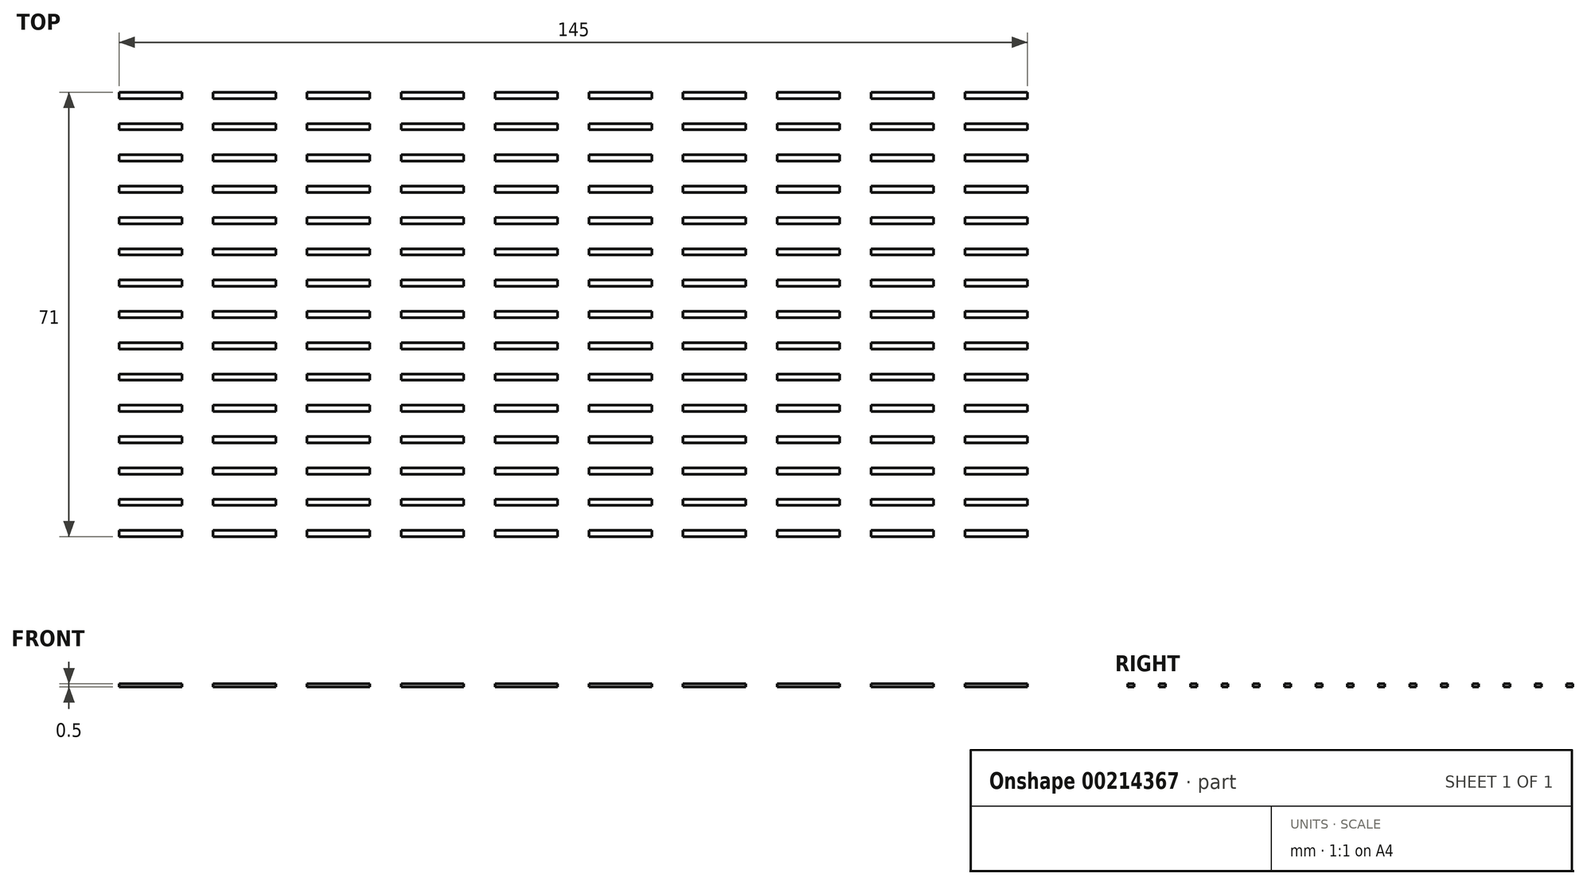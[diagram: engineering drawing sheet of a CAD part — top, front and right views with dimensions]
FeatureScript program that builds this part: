
annotation { "Feature Type Name" : "Feature", "Feature Type Description" : "" }
export const myFeature = defineFeature(function(context is Context, id is Id, definition is map)
    precondition{}
    {
        {
            var Q0;
            Q0=qCreatedBy(makeId("Top.planeOp"),FACE);
            var sketch = newSketch(context, id + "F0", { "sketchPlane" : qUnion([Q0])});
            skLineSegment(sketch, "E0.bottom", {"start": v(0, 0) * mm, "end": v(10, 0) * mm});
            skLineSegment(sketch, "E0.top", {"start": v(0, 1) * mm, "end": v(10, 1) * mm});
            skLineSegment(sketch, "E0.left", {"start": v(0, 0) * mm, "end": v(0, 1) * mm});
            skLineSegment(sketch, "E0.right", {"start": v(10, 0) * mm, "end": v(10, 1) * mm});
            skLineSegment(sketch, "E1.0.1.0", {"start": v(0, 6) * mm, "end": v(10, 6) * mm});
            skLineSegment(sketch, "E1.0.1.1", {"start": v(0, 5) * mm, "end": v(0, 6) * mm});
            skLineSegment(sketch, "E1.0.1.2", {"start": v(10, 5) * mm, "end": v(10, 6) * mm});
            skLineSegment(sketch, "E1.0.1.3", {"start": v(0, 5) * mm, "end": v(10, 5) * mm});
            skLineSegment(sketch, "E1.1.0.0", {"start": v(15, 1) * mm, "end": v(25, 1) * mm});
            skLineSegment(sketch, "E1.1.0.1", {"start": v(15, 0) * mm, "end": v(15, 1) * mm});
            skLineSegment(sketch, "E1.1.0.2", {"start": v(25, 0) * mm, "end": v(25, 1) * mm});
            skLineSegment(sketch, "E1.1.0.3", {"start": v(15, 0) * mm, "end": v(25, 0) * mm});
            skLineSegment(sketch, "E1.1.1.0", {"start": v(15, 6) * mm, "end": v(25, 6) * mm});
            skLineSegment(sketch, "E1.1.1.1", {"start": v(15, 5) * mm, "end": v(15, 6) * mm});
            skLineSegment(sketch, "E1.1.1.2", {"start": v(25, 5) * mm, "end": v(25, 6) * mm});
            skLineSegment(sketch, "E1.1.1.3", {"start": v(15, 5) * mm, "end": v(25, 5) * mm});
            skLineSegment(sketch, "E1.2.0.0", {"start": v(30, 1) * mm, "end": v(40, 1) * mm});
            skLineSegment(sketch, "E1.2.0.1", {"start": v(30, 0) * mm, "end": v(30, 1) * mm});
            skLineSegment(sketch, "E1.2.0.2", {"start": v(40, 0) * mm, "end": v(40, 1) * mm});
            skLineSegment(sketch, "E1.2.0.3", {"start": v(30, 0) * mm, "end": v(40, 0) * mm});
            skLineSegment(sketch, "E1.2.1.0", {"start": v(30, 6) * mm, "end": v(40, 6) * mm});
            skLineSegment(sketch, "E1.2.1.1", {"start": v(30, 5) * mm, "end": v(30, 6) * mm});
            skLineSegment(sketch, "E1.2.1.2", {"start": v(40, 5) * mm, "end": v(40, 6) * mm});
            skLineSegment(sketch, "E1.2.1.3", {"start": v(30, 5) * mm, "end": v(40, 5) * mm});
            skLineSegment(sketch, "E1.direction1", {"start": v(0, 0) * mm, "end": v(15, 0) * mm, "construction": true});
            skLineSegment(sketch, "E1.direction2", {"start": v(0, 0) * mm, "end": v(0, 5) * mm, "construction": true});
            skLineSegment(sketch, "E2.0.3.0", {"start": v(45, 1) * mm, "end": v(55, 1) * mm});
            skLineSegment(sketch, "E2.3.3.0", {"start": v(45, 0) * mm, "end": v(45, 1) * mm});
            skLineSegment(sketch, "E2.6.3.0", {"start": v(55, 0) * mm, "end": v(55, 1) * mm});
            skLineSegment(sketch, "E2.9.3.0", {"start": v(45, 0) * mm, "end": v(55, 0) * mm});
            skLineSegment(sketch, "E2.0.3.1", {"start": v(45, 6) * mm, "end": v(55, 6) * mm});
            skLineSegment(sketch, "E2.3.3.1", {"start": v(45, 5) * mm, "end": v(45, 6) * mm});
            skLineSegment(sketch, "E2.6.3.1", {"start": v(55, 5) * mm, "end": v(55, 6) * mm});
            skLineSegment(sketch, "E2.9.3.1", {"start": v(45, 5) * mm, "end": v(55, 5) * mm});
            skLineSegment(sketch, "E2.0.4.0", {"start": v(60, 1) * mm, "end": v(70, 1) * mm});
            skLineSegment(sketch, "E2.3.4.0", {"start": v(60, 0) * mm, "end": v(60, 1) * mm});
            skLineSegment(sketch, "E2.6.4.0", {"start": v(70, 0) * mm, "end": v(70, 1) * mm});
            skLineSegment(sketch, "E2.9.4.0", {"start": v(60, 0) * mm, "end": v(70, 0) * mm});
            skLineSegment(sketch, "E2.0.4.1", {"start": v(60, 6) * mm, "end": v(70, 6) * mm});
            skLineSegment(sketch, "E2.3.4.1", {"start": v(60, 5) * mm, "end": v(60, 6) * mm});
            skLineSegment(sketch, "E2.6.4.1", {"start": v(70, 5) * mm, "end": v(70, 6) * mm});
            skLineSegment(sketch, "E2.9.4.1", {"start": v(60, 5) * mm, "end": v(70, 5) * mm});
            skLineSegment(sketch, "E2.0.5.0", {"start": v(75, 1) * mm, "end": v(85, 1) * mm});
            skLineSegment(sketch, "E2.3.5.0", {"start": v(75, 0) * mm, "end": v(75, 1) * mm});
            skLineSegment(sketch, "E2.6.5.0", {"start": v(85, 0) * mm, "end": v(85, 1) * mm});
            skLineSegment(sketch, "E2.9.5.0", {"start": v(75, 0) * mm, "end": v(85, 0) * mm});
            skLineSegment(sketch, "E2.0.5.1", {"start": v(75, 6) * mm, "end": v(85, 6) * mm});
            skLineSegment(sketch, "E2.3.5.1", {"start": v(75, 5) * mm, "end": v(75, 6) * mm});
            skLineSegment(sketch, "E2.6.5.1", {"start": v(85, 5) * mm, "end": v(85, 6) * mm});
            skLineSegment(sketch, "E2.9.5.1", {"start": v(75, 5) * mm, "end": v(85, 5) * mm});
            skLineSegment(sketch, "E2.0.6.0", {"start": v(90, 1) * mm, "end": v(100, 1) * mm});
            skLineSegment(sketch, "E2.3.6.0", {"start": v(90, 0) * mm, "end": v(90, 1) * mm});
            skLineSegment(sketch, "E2.6.6.0", {"start": v(100, 0) * mm, "end": v(100, 1) * mm});
            skLineSegment(sketch, "E2.9.6.0", {"start": v(90, 0) * mm, "end": v(100, 0) * mm});
            skLineSegment(sketch, "E2.0.6.1", {"start": v(90, 6) * mm, "end": v(100, 6) * mm});
            skLineSegment(sketch, "E2.3.6.1", {"start": v(90, 5) * mm, "end": v(90, 6) * mm});
            skLineSegment(sketch, "E2.6.6.1", {"start": v(100, 5) * mm, "end": v(100, 6) * mm});
            skLineSegment(sketch, "E2.9.6.1", {"start": v(90, 5) * mm, "end": v(100, 5) * mm});
            skLineSegment(sketch, "E2.0.7.0", {"start": v(105, 1) * mm, "end": v(115, 1) * mm});
            skLineSegment(sketch, "E2.3.7.0", {"start": v(105, 0) * mm, "end": v(105, 1) * mm});
            skLineSegment(sketch, "E2.6.7.0", {"start": v(115, 0) * mm, "end": v(115, 1) * mm});
            skLineSegment(sketch, "E2.9.7.0", {"start": v(105, 0) * mm, "end": v(115, 0) * mm});
            skLineSegment(sketch, "E2.0.7.1", {"start": v(105, 6) * mm, "end": v(115, 6) * mm});
            skLineSegment(sketch, "E2.3.7.1", {"start": v(105, 5) * mm, "end": v(105, 6) * mm});
            skLineSegment(sketch, "E2.6.7.1", {"start": v(115, 5) * mm, "end": v(115, 6) * mm});
            skLineSegment(sketch, "E2.9.7.1", {"start": v(105, 5) * mm, "end": v(115, 5) * mm});
            skLineSegment(sketch, "E2.0.8.0", {"start": v(120, 1) * mm, "end": v(130, 1) * mm});
            skLineSegment(sketch, "E2.3.8.0", {"start": v(120, 0) * mm, "end": v(120, 1) * mm});
            skLineSegment(sketch, "E2.6.8.0", {"start": v(130, 0) * mm, "end": v(130, 1) * mm});
            skLineSegment(sketch, "E2.9.8.0", {"start": v(120, 0) * mm, "end": v(130, 0) * mm});
            skLineSegment(sketch, "E2.0.8.1", {"start": v(120, 6) * mm, "end": v(130, 6) * mm});
            skLineSegment(sketch, "E2.3.8.1", {"start": v(120, 5) * mm, "end": v(120, 6) * mm});
            skLineSegment(sketch, "E2.6.8.1", {"start": v(130, 5) * mm, "end": v(130, 6) * mm});
            skLineSegment(sketch, "E2.9.8.1", {"start": v(120, 5) * mm, "end": v(130, 5) * mm});
            skLineSegment(sketch, "E2.0.9.0", {"start": v(135, 1) * mm, "end": v(145, 1) * mm});
            skLineSegment(sketch, "E2.3.9.0", {"start": v(135, 0) * mm, "end": v(135, 1) * mm});
            skLineSegment(sketch, "E2.6.9.0", {"start": v(145, 0) * mm, "end": v(145, 1) * mm});
            skLineSegment(sketch, "E2.9.9.0", {"start": v(135, 0) * mm, "end": v(145, 0) * mm});
            skLineSegment(sketch, "E2.0.9.1", {"start": v(135, 6) * mm, "end": v(145, 6) * mm});
            skLineSegment(sketch, "E2.3.9.1", {"start": v(135, 5) * mm, "end": v(135, 6) * mm});
            skLineSegment(sketch, "E2.6.9.1", {"start": v(145, 5) * mm, "end": v(145, 6) * mm});
            skLineSegment(sketch, "E2.9.9.1", {"start": v(135, 5) * mm, "end": v(145, 5) * mm});
            skLineSegment(sketch, "E3.0.0.2", {"start": v(0, 11) * mm, "end": v(10, 11) * mm});
            skLineSegment(sketch, "E3.3.0.2", {"start": v(0, 10) * mm, "end": v(0, 11) * mm});
            skLineSegment(sketch, "E3.6.0.2", {"start": v(10, 10) * mm, "end": v(10, 11) * mm});
            skLineSegment(sketch, "E3.9.0.2", {"start": v(0, 10) * mm, "end": v(10, 10) * mm});
            skLineSegment(sketch, "E3.0.0.3", {"start": v(0, 16) * mm, "end": v(10, 16) * mm});
            skLineSegment(sketch, "E3.3.0.3", {"start": v(0, 15) * mm, "end": v(0, 16) * mm});
            skLineSegment(sketch, "E3.6.0.3", {"start": v(10, 15) * mm, "end": v(10, 16) * mm});
            skLineSegment(sketch, "E3.9.0.3", {"start": v(0, 15) * mm, "end": v(10, 15) * mm});
            skLineSegment(sketch, "E3.0.0.4", {"start": v(0, 21) * mm, "end": v(10, 21) * mm});
            skLineSegment(sketch, "E3.3.0.4", {"start": v(0, 20) * mm, "end": v(0, 21) * mm});
            skLineSegment(sketch, "E3.6.0.4", {"start": v(10, 20) * mm, "end": v(10, 21) * mm});
            skLineSegment(sketch, "E3.9.0.4", {"start": v(0, 20) * mm, "end": v(10, 20) * mm});
            skLineSegment(sketch, "E3.0.0.5", {"start": v(0, 26) * mm, "end": v(10, 26) * mm});
            skLineSegment(sketch, "E3.3.0.5", {"start": v(0, 25) * mm, "end": v(0, 26) * mm});
            skLineSegment(sketch, "E3.6.0.5", {"start": v(10, 25) * mm, "end": v(10, 26) * mm});
            skLineSegment(sketch, "E3.9.0.5", {"start": v(0, 25) * mm, "end": v(10, 25) * mm});
            skLineSegment(sketch, "E3.0.0.6", {"start": v(0, 31) * mm, "end": v(10, 31) * mm});
            skLineSegment(sketch, "E3.3.0.6", {"start": v(0, 30) * mm, "end": v(0, 31) * mm});
            skLineSegment(sketch, "E3.6.0.6", {"start": v(10, 30) * mm, "end": v(10, 31) * mm});
            skLineSegment(sketch, "E3.9.0.6", {"start": v(0, 30) * mm, "end": v(10, 30) * mm});
            skLineSegment(sketch, "E3.0.0.7", {"start": v(0, 36) * mm, "end": v(10, 36) * mm});
            skLineSegment(sketch, "E3.3.0.7", {"start": v(0, 35) * mm, "end": v(0, 36) * mm});
            skLineSegment(sketch, "E3.6.0.7", {"start": v(10, 35) * mm, "end": v(10, 36) * mm});
            skLineSegment(sketch, "E3.9.0.7", {"start": v(0, 35) * mm, "end": v(10, 35) * mm});
            skLineSegment(sketch, "E3.0.0.8", {"start": v(0, 41) * mm, "end": v(10, 41) * mm});
            skLineSegment(sketch, "E3.3.0.8", {"start": v(0, 40) * mm, "end": v(0, 41) * mm});
            skLineSegment(sketch, "E3.6.0.8", {"start": v(10, 40) * mm, "end": v(10, 41) * mm});
            skLineSegment(sketch, "E3.9.0.8", {"start": v(0, 40) * mm, "end": v(10, 40) * mm});
            skLineSegment(sketch, "E3.0.0.9", {"start": v(0, 46) * mm, "end": v(10, 46) * mm});
            skLineSegment(sketch, "E3.3.0.9", {"start": v(0, 45) * mm, "end": v(0, 46) * mm});
            skLineSegment(sketch, "E3.6.0.9", {"start": v(10, 45) * mm, "end": v(10, 46) * mm});
            skLineSegment(sketch, "E3.9.0.9", {"start": v(0, 45) * mm, "end": v(10, 45) * mm});
            skLineSegment(sketch, "E3.0.1.2", {"start": v(15, 11) * mm, "end": v(25, 11) * mm});
            skLineSegment(sketch, "E3.3.1.2", {"start": v(15, 10) * mm, "end": v(15, 11) * mm});
            skLineSegment(sketch, "E3.6.1.2", {"start": v(25, 10) * mm, "end": v(25, 11) * mm});
            skLineSegment(sketch, "E3.9.1.2", {"start": v(15, 10) * mm, "end": v(25, 10) * mm});
            skLineSegment(sketch, "E3.0.1.3", {"start": v(15, 16) * mm, "end": v(25, 16) * mm});
            skLineSegment(sketch, "E3.3.1.3", {"start": v(15, 15) * mm, "end": v(15, 16) * mm});
            skLineSegment(sketch, "E3.6.1.3", {"start": v(25, 15) * mm, "end": v(25, 16) * mm});
            skLineSegment(sketch, "E3.9.1.3", {"start": v(15, 15) * mm, "end": v(25, 15) * mm});
            skLineSegment(sketch, "E3.0.1.4", {"start": v(15, 21) * mm, "end": v(25, 21) * mm});
            skLineSegment(sketch, "E3.3.1.4", {"start": v(15, 20) * mm, "end": v(15, 21) * mm});
            skLineSegment(sketch, "E3.6.1.4", {"start": v(25, 20) * mm, "end": v(25, 21) * mm});
            skLineSegment(sketch, "E3.9.1.4", {"start": v(15, 20) * mm, "end": v(25, 20) * mm});
            skLineSegment(sketch, "E3.0.1.5", {"start": v(15, 26) * mm, "end": v(25, 26) * mm});
            skLineSegment(sketch, "E3.3.1.5", {"start": v(15, 25) * mm, "end": v(15, 26) * mm});
            skLineSegment(sketch, "E3.6.1.5", {"start": v(25, 25) * mm, "end": v(25, 26) * mm});
            skLineSegment(sketch, "E3.9.1.5", {"start": v(15, 25) * mm, "end": v(25, 25) * mm});
            skLineSegment(sketch, "E3.0.1.6", {"start": v(15, 31) * mm, "end": v(25, 31) * mm});
            skLineSegment(sketch, "E3.3.1.6", {"start": v(15, 30) * mm, "end": v(15, 31) * mm});
            skLineSegment(sketch, "E3.6.1.6", {"start": v(25, 30) * mm, "end": v(25, 31) * mm});
            skLineSegment(sketch, "E3.9.1.6", {"start": v(15, 30) * mm, "end": v(25, 30) * mm});
            skLineSegment(sketch, "E3.0.1.7", {"start": v(15, 36) * mm, "end": v(25, 36) * mm});
            skLineSegment(sketch, "E3.3.1.7", {"start": v(15, 35) * mm, "end": v(15, 36) * mm});
            skLineSegment(sketch, "E3.6.1.7", {"start": v(25, 35) * mm, "end": v(25, 36) * mm});
            skLineSegment(sketch, "E3.9.1.7", {"start": v(15, 35) * mm, "end": v(25, 35) * mm});
            skLineSegment(sketch, "E3.0.1.8", {"start": v(15, 41) * mm, "end": v(25, 41) * mm});
            skLineSegment(sketch, "E3.3.1.8", {"start": v(15, 40) * mm, "end": v(15, 41) * mm});
            skLineSegment(sketch, "E3.6.1.8", {"start": v(25, 40) * mm, "end": v(25, 41) * mm});
            skLineSegment(sketch, "E3.9.1.8", {"start": v(15, 40) * mm, "end": v(25, 40) * mm});
            skLineSegment(sketch, "E3.0.1.9", {"start": v(15, 46) * mm, "end": v(25, 46) * mm});
            skLineSegment(sketch, "E3.3.1.9", {"start": v(15, 45) * mm, "end": v(15, 46) * mm});
            skLineSegment(sketch, "E3.6.1.9", {"start": v(25, 45) * mm, "end": v(25, 46) * mm});
            skLineSegment(sketch, "E3.9.1.9", {"start": v(15, 45) * mm, "end": v(25, 45) * mm});
            skLineSegment(sketch, "E3.0.2.2", {"start": v(30, 11) * mm, "end": v(40, 11) * mm});
            skLineSegment(sketch, "E3.3.2.2", {"start": v(30, 10) * mm, "end": v(30, 11) * mm});
            skLineSegment(sketch, "E3.6.2.2", {"start": v(40, 10) * mm, "end": v(40, 11) * mm});
            skLineSegment(sketch, "E3.9.2.2", {"start": v(30, 10) * mm, "end": v(40, 10) * mm});
            skLineSegment(sketch, "E3.0.2.3", {"start": v(30, 16) * mm, "end": v(40, 16) * mm});
            skLineSegment(sketch, "E3.3.2.3", {"start": v(30, 15) * mm, "end": v(30, 16) * mm});
            skLineSegment(sketch, "E3.6.2.3", {"start": v(40, 15) * mm, "end": v(40, 16) * mm});
            skLineSegment(sketch, "E3.9.2.3", {"start": v(30, 15) * mm, "end": v(40, 15) * mm});
            skLineSegment(sketch, "E3.0.2.4", {"start": v(30, 21) * mm, "end": v(40, 21) * mm});
            skLineSegment(sketch, "E3.3.2.4", {"start": v(30, 20) * mm, "end": v(30, 21) * mm});
            skLineSegment(sketch, "E3.6.2.4", {"start": v(40, 20) * mm, "end": v(40, 21) * mm});
            skLineSegment(sketch, "E3.9.2.4", {"start": v(30, 20) * mm, "end": v(40, 20) * mm});
            skLineSegment(sketch, "E3.0.2.5", {"start": v(30, 26) * mm, "end": v(40, 26) * mm});
            skLineSegment(sketch, "E3.3.2.5", {"start": v(30, 25) * mm, "end": v(30, 26) * mm});
            skLineSegment(sketch, "E3.6.2.5", {"start": v(40, 25) * mm, "end": v(40, 26) * mm});
            skLineSegment(sketch, "E3.9.2.5", {"start": v(30, 25) * mm, "end": v(40, 25) * mm});
            skLineSegment(sketch, "E3.0.2.6", {"start": v(30, 31) * mm, "end": v(40, 31) * mm});
            skLineSegment(sketch, "E3.3.2.6", {"start": v(30, 30) * mm, "end": v(30, 31) * mm});
            skLineSegment(sketch, "E3.6.2.6", {"start": v(40, 30) * mm, "end": v(40, 31) * mm});
            skLineSegment(sketch, "E3.9.2.6", {"start": v(30, 30) * mm, "end": v(40, 30) * mm});
            skLineSegment(sketch, "E3.0.2.7", {"start": v(30, 36) * mm, "end": v(40, 36) * mm});
            skLineSegment(sketch, "E3.3.2.7", {"start": v(30, 35) * mm, "end": v(30, 36) * mm});
            skLineSegment(sketch, "E3.6.2.7", {"start": v(40, 35) * mm, "end": v(40, 36) * mm});
            skLineSegment(sketch, "E3.9.2.7", {"start": v(30, 35) * mm, "end": v(40, 35) * mm});
            skLineSegment(sketch, "E3.0.2.8", {"start": v(30, 41) * mm, "end": v(40, 41) * mm});
            skLineSegment(sketch, "E3.3.2.8", {"start": v(30, 40) * mm, "end": v(30, 41) * mm});
            skLineSegment(sketch, "E3.6.2.8", {"start": v(40, 40) * mm, "end": v(40, 41) * mm});
            skLineSegment(sketch, "E3.9.2.8", {"start": v(30, 40) * mm, "end": v(40, 40) * mm});
            skLineSegment(sketch, "E3.0.2.9", {"start": v(30, 46) * mm, "end": v(40, 46) * mm});
            skLineSegment(sketch, "E3.3.2.9", {"start": v(30, 45) * mm, "end": v(30, 46) * mm});
            skLineSegment(sketch, "E3.6.2.9", {"start": v(40, 45) * mm, "end": v(40, 46) * mm});
            skLineSegment(sketch, "E3.9.2.9", {"start": v(30, 45) * mm, "end": v(40, 45) * mm});
            skLineSegment(sketch, "E3.0.3.2", {"start": v(45, 11) * mm, "end": v(55, 11) * mm});
            skLineSegment(sketch, "E3.3.3.2", {"start": v(45, 10) * mm, "end": v(45, 11) * mm});
            skLineSegment(sketch, "E3.6.3.2", {"start": v(55, 10) * mm, "end": v(55, 11) * mm});
            skLineSegment(sketch, "E3.9.3.2", {"start": v(45, 10) * mm, "end": v(55, 10) * mm});
            skLineSegment(sketch, "E3.0.3.3", {"start": v(45, 16) * mm, "end": v(55, 16) * mm});
            skLineSegment(sketch, "E3.3.3.3", {"start": v(45, 15) * mm, "end": v(45, 16) * mm});
            skLineSegment(sketch, "E3.6.3.3", {"start": v(55, 15) * mm, "end": v(55, 16) * mm});
            skLineSegment(sketch, "E3.9.3.3", {"start": v(45, 15) * mm, "end": v(55, 15) * mm});
            skLineSegment(sketch, "E3.0.3.4", {"start": v(45, 21) * mm, "end": v(55, 21) * mm});
            skLineSegment(sketch, "E3.3.3.4", {"start": v(45, 20) * mm, "end": v(45, 21) * mm});
            skLineSegment(sketch, "E3.6.3.4", {"start": v(55, 20) * mm, "end": v(55, 21) * mm});
            skLineSegment(sketch, "E3.9.3.4", {"start": v(45, 20) * mm, "end": v(55, 20) * mm});
            skLineSegment(sketch, "E3.0.3.5", {"start": v(45, 26) * mm, "end": v(55, 26) * mm});
            skLineSegment(sketch, "E3.3.3.5", {"start": v(45, 25) * mm, "end": v(45, 26) * mm});
            skLineSegment(sketch, "E3.6.3.5", {"start": v(55, 25) * mm, "end": v(55, 26) * mm});
            skLineSegment(sketch, "E3.9.3.5", {"start": v(45, 25) * mm, "end": v(55, 25) * mm});
            skLineSegment(sketch, "E3.0.3.6", {"start": v(45, 31) * mm, "end": v(55, 31) * mm});
            skLineSegment(sketch, "E3.3.3.6", {"start": v(45, 30) * mm, "end": v(45, 31) * mm});
            skLineSegment(sketch, "E3.6.3.6", {"start": v(55, 30) * mm, "end": v(55, 31) * mm});
            skLineSegment(sketch, "E3.9.3.6", {"start": v(45, 30) * mm, "end": v(55, 30) * mm});
            skLineSegment(sketch, "E3.0.3.7", {"start": v(45, 36) * mm, "end": v(55, 36) * mm});
            skLineSegment(sketch, "E3.3.3.7", {"start": v(45, 35) * mm, "end": v(45, 36) * mm});
            skLineSegment(sketch, "E3.6.3.7", {"start": v(55, 35) * mm, "end": v(55, 36) * mm});
            skLineSegment(sketch, "E3.9.3.7", {"start": v(45, 35) * mm, "end": v(55, 35) * mm});
            skLineSegment(sketch, "E3.0.3.8", {"start": v(45, 41) * mm, "end": v(55, 41) * mm});
            skLineSegment(sketch, "E3.3.3.8", {"start": v(45, 40) * mm, "end": v(45, 41) * mm});
            skLineSegment(sketch, "E3.6.3.8", {"start": v(55, 40) * mm, "end": v(55, 41) * mm});
            skLineSegment(sketch, "E3.9.3.8", {"start": v(45, 40) * mm, "end": v(55, 40) * mm});
            skLineSegment(sketch, "E3.0.3.9", {"start": v(45, 46) * mm, "end": v(55, 46) * mm});
            skLineSegment(sketch, "E3.3.3.9", {"start": v(45, 45) * mm, "end": v(45, 46) * mm});
            skLineSegment(sketch, "E3.6.3.9", {"start": v(55, 45) * mm, "end": v(55, 46) * mm});
            skLineSegment(sketch, "E3.9.3.9", {"start": v(45, 45) * mm, "end": v(55, 45) * mm});
            skLineSegment(sketch, "E3.0.4.2", {"start": v(60, 11) * mm, "end": v(70, 11) * mm});
            skLineSegment(sketch, "E3.3.4.2", {"start": v(60, 10) * mm, "end": v(60, 11) * mm});
            skLineSegment(sketch, "E3.6.4.2", {"start": v(70, 10) * mm, "end": v(70, 11) * mm});
            skLineSegment(sketch, "E3.9.4.2", {"start": v(60, 10) * mm, "end": v(70, 10) * mm});
            skLineSegment(sketch, "E3.0.4.3", {"start": v(60, 16) * mm, "end": v(70, 16) * mm});
            skLineSegment(sketch, "E3.3.4.3", {"start": v(60, 15) * mm, "end": v(60, 16) * mm});
            skLineSegment(sketch, "E3.6.4.3", {"start": v(70, 15) * mm, "end": v(70, 16) * mm});
            skLineSegment(sketch, "E3.9.4.3", {"start": v(60, 15) * mm, "end": v(70, 15) * mm});
            skLineSegment(sketch, "E3.0.4.4", {"start": v(60, 21) * mm, "end": v(70, 21) * mm});
            skLineSegment(sketch, "E3.3.4.4", {"start": v(60, 20) * mm, "end": v(60, 21) * mm});
            skLineSegment(sketch, "E3.6.4.4", {"start": v(70, 20) * mm, "end": v(70, 21) * mm});
            skLineSegment(sketch, "E3.9.4.4", {"start": v(60, 20) * mm, "end": v(70, 20) * mm});
            skLineSegment(sketch, "E3.0.4.5", {"start": v(60, 26) * mm, "end": v(70, 26) * mm});
            skLineSegment(sketch, "E3.3.4.5", {"start": v(60, 25) * mm, "end": v(60, 26) * mm});
            skLineSegment(sketch, "E3.6.4.5", {"start": v(70, 25) * mm, "end": v(70, 26) * mm});
            skLineSegment(sketch, "E3.9.4.5", {"start": v(60, 25) * mm, "end": v(70, 25) * mm});
            skLineSegment(sketch, "E3.0.4.6", {"start": v(60, 31) * mm, "end": v(70, 31) * mm});
            skLineSegment(sketch, "E3.3.4.6", {"start": v(60, 30) * mm, "end": v(60, 31) * mm});
            skLineSegment(sketch, "E3.6.4.6", {"start": v(70, 30) * mm, "end": v(70, 31) * mm});
            skLineSegment(sketch, "E3.9.4.6", {"start": v(60, 30) * mm, "end": v(70, 30) * mm});
            skLineSegment(sketch, "E3.0.4.7", {"start": v(60, 36) * mm, "end": v(70, 36) * mm});
            skLineSegment(sketch, "E3.3.4.7", {"start": v(60, 35) * mm, "end": v(60, 36) * mm});
            skLineSegment(sketch, "E3.6.4.7", {"start": v(70, 35) * mm, "end": v(70, 36) * mm});
            skLineSegment(sketch, "E3.9.4.7", {"start": v(60, 35) * mm, "end": v(70, 35) * mm});
            skLineSegment(sketch, "E3.0.4.8", {"start": v(60, 41) * mm, "end": v(70, 41) * mm});
            skLineSegment(sketch, "E3.3.4.8", {"start": v(60, 40) * mm, "end": v(60, 41) * mm});
            skLineSegment(sketch, "E3.6.4.8", {"start": v(70, 40) * mm, "end": v(70, 41) * mm});
            skLineSegment(sketch, "E3.9.4.8", {"start": v(60, 40) * mm, "end": v(70, 40) * mm});
            skLineSegment(sketch, "E3.0.4.9", {"start": v(60, 46) * mm, "end": v(70, 46) * mm});
            skLineSegment(sketch, "E3.3.4.9", {"start": v(60, 45) * mm, "end": v(60, 46) * mm});
            skLineSegment(sketch, "E3.6.4.9", {"start": v(70, 45) * mm, "end": v(70, 46) * mm});
            skLineSegment(sketch, "E3.9.4.9", {"start": v(60, 45) * mm, "end": v(70, 45) * mm});
            skLineSegment(sketch, "E3.0.5.2", {"start": v(75, 11) * mm, "end": v(85, 11) * mm});
            skLineSegment(sketch, "E3.3.5.2", {"start": v(75, 10) * mm, "end": v(75, 11) * mm});
            skLineSegment(sketch, "E3.6.5.2", {"start": v(85, 10) * mm, "end": v(85, 11) * mm});
            skLineSegment(sketch, "E3.9.5.2", {"start": v(75, 10) * mm, "end": v(85, 10) * mm});
            skLineSegment(sketch, "E3.0.5.3", {"start": v(75, 16) * mm, "end": v(85, 16) * mm});
            skLineSegment(sketch, "E3.3.5.3", {"start": v(75, 15) * mm, "end": v(75, 16) * mm});
            skLineSegment(sketch, "E3.6.5.3", {"start": v(85, 15) * mm, "end": v(85, 16) * mm});
            skLineSegment(sketch, "E3.9.5.3", {"start": v(75, 15) * mm, "end": v(85, 15) * mm});
            skLineSegment(sketch, "E3.0.5.4", {"start": v(75, 21) * mm, "end": v(85, 21) * mm});
            skLineSegment(sketch, "E3.3.5.4", {"start": v(75, 20) * mm, "end": v(75, 21) * mm});
            skLineSegment(sketch, "E3.6.5.4", {"start": v(85, 20) * mm, "end": v(85, 21) * mm});
            skLineSegment(sketch, "E3.9.5.4", {"start": v(75, 20) * mm, "end": v(85, 20) * mm});
            skLineSegment(sketch, "E3.0.5.5", {"start": v(75, 26) * mm, "end": v(85, 26) * mm});
            skLineSegment(sketch, "E3.3.5.5", {"start": v(75, 25) * mm, "end": v(75, 26) * mm});
            skLineSegment(sketch, "E3.6.5.5", {"start": v(85, 25) * mm, "end": v(85, 26) * mm});
            skLineSegment(sketch, "E3.9.5.5", {"start": v(75, 25) * mm, "end": v(85, 25) * mm});
            skLineSegment(sketch, "E3.0.5.6", {"start": v(75, 31) * mm, "end": v(85, 31) * mm});
            skLineSegment(sketch, "E3.3.5.6", {"start": v(75, 30) * mm, "end": v(75, 31) * mm});
            skLineSegment(sketch, "E3.6.5.6", {"start": v(85, 30) * mm, "end": v(85, 31) * mm});
            skLineSegment(sketch, "E3.9.5.6", {"start": v(75, 30) * mm, "end": v(85, 30) * mm});
            skLineSegment(sketch, "E3.0.5.7", {"start": v(75, 36) * mm, "end": v(85, 36) * mm});
            skLineSegment(sketch, "E3.3.5.7", {"start": v(75, 35) * mm, "end": v(75, 36) * mm});
            skLineSegment(sketch, "E3.6.5.7", {"start": v(85, 35) * mm, "end": v(85, 36) * mm});
            skLineSegment(sketch, "E3.9.5.7", {"start": v(75, 35) * mm, "end": v(85, 35) * mm});
            skLineSegment(sketch, "E3.0.5.8", {"start": v(75, 41) * mm, "end": v(85, 41) * mm});
            skLineSegment(sketch, "E3.3.5.8", {"start": v(75, 40) * mm, "end": v(75, 41) * mm});
            skLineSegment(sketch, "E3.6.5.8", {"start": v(85, 40) * mm, "end": v(85, 41) * mm});
            skLineSegment(sketch, "E3.9.5.8", {"start": v(75, 40) * mm, "end": v(85, 40) * mm});
            skLineSegment(sketch, "E3.0.5.9", {"start": v(75, 46) * mm, "end": v(85, 46) * mm});
            skLineSegment(sketch, "E3.3.5.9", {"start": v(75, 45) * mm, "end": v(75, 46) * mm});
            skLineSegment(sketch, "E3.6.5.9", {"start": v(85, 45) * mm, "end": v(85, 46) * mm});
            skLineSegment(sketch, "E3.9.5.9", {"start": v(75, 45) * mm, "end": v(85, 45) * mm});
            skLineSegment(sketch, "E3.0.6.2", {"start": v(90, 11) * mm, "end": v(100, 11) * mm});
            skLineSegment(sketch, "E3.3.6.2", {"start": v(90, 10) * mm, "end": v(90, 11) * mm});
            skLineSegment(sketch, "E3.6.6.2", {"start": v(100, 10) * mm, "end": v(100, 11) * mm});
            skLineSegment(sketch, "E3.9.6.2", {"start": v(90, 10) * mm, "end": v(100, 10) * mm});
            skLineSegment(sketch, "E3.0.6.3", {"start": v(90, 16) * mm, "end": v(100, 16) * mm});
            skLineSegment(sketch, "E3.3.6.3", {"start": v(90, 15) * mm, "end": v(90, 16) * mm});
            skLineSegment(sketch, "E3.6.6.3", {"start": v(100, 15) * mm, "end": v(100, 16) * mm});
            skLineSegment(sketch, "E3.9.6.3", {"start": v(90, 15) * mm, "end": v(100, 15) * mm});
            skLineSegment(sketch, "E3.0.6.4", {"start": v(90, 21) * mm, "end": v(100, 21) * mm});
            skLineSegment(sketch, "E3.3.6.4", {"start": v(90, 20) * mm, "end": v(90, 21) * mm});
            skLineSegment(sketch, "E3.6.6.4", {"start": v(100, 20) * mm, "end": v(100, 21) * mm});
            skLineSegment(sketch, "E3.9.6.4", {"start": v(90, 20) * mm, "end": v(100, 20) * mm});
            skLineSegment(sketch, "E3.0.6.5", {"start": v(90, 26) * mm, "end": v(100, 26) * mm});
            skLineSegment(sketch, "E3.3.6.5", {"start": v(90, 25) * mm, "end": v(90, 26) * mm});
            skLineSegment(sketch, "E3.6.6.5", {"start": v(100, 25) * mm, "end": v(100, 26) * mm});
            skLineSegment(sketch, "E3.9.6.5", {"start": v(90, 25) * mm, "end": v(100, 25) * mm});
            skLineSegment(sketch, "E3.0.6.6", {"start": v(90, 31) * mm, "end": v(100, 31) * mm});
            skLineSegment(sketch, "E3.3.6.6", {"start": v(90, 30) * mm, "end": v(90, 31) * mm});
            skLineSegment(sketch, "E3.6.6.6", {"start": v(100, 30) * mm, "end": v(100, 31) * mm});
            skLineSegment(sketch, "E3.9.6.6", {"start": v(90, 30) * mm, "end": v(100, 30) * mm});
            skLineSegment(sketch, "E3.0.6.7", {"start": v(90, 36) * mm, "end": v(100, 36) * mm});
            skLineSegment(sketch, "E3.3.6.7", {"start": v(90, 35) * mm, "end": v(90, 36) * mm});
            skLineSegment(sketch, "E3.6.6.7", {"start": v(100, 35) * mm, "end": v(100, 36) * mm});
            skLineSegment(sketch, "E3.9.6.7", {"start": v(90, 35) * mm, "end": v(100, 35) * mm});
            skLineSegment(sketch, "E3.0.6.8", {"start": v(90, 41) * mm, "end": v(100, 41) * mm});
            skLineSegment(sketch, "E3.3.6.8", {"start": v(90, 40) * mm, "end": v(90, 41) * mm});
            skLineSegment(sketch, "E3.6.6.8", {"start": v(100, 40) * mm, "end": v(100, 41) * mm});
            skLineSegment(sketch, "E3.9.6.8", {"start": v(90, 40) * mm, "end": v(100, 40) * mm});
            skLineSegment(sketch, "E3.0.6.9", {"start": v(90, 46) * mm, "end": v(100, 46) * mm});
            skLineSegment(sketch, "E3.3.6.9", {"start": v(90, 45) * mm, "end": v(90, 46) * mm});
            skLineSegment(sketch, "E3.6.6.9", {"start": v(100, 45) * mm, "end": v(100, 46) * mm});
            skLineSegment(sketch, "E3.9.6.9", {"start": v(90, 45) * mm, "end": v(100, 45) * mm});
            skLineSegment(sketch, "E3.0.7.2", {"start": v(105, 11) * mm, "end": v(115, 11) * mm});
            skLineSegment(sketch, "E3.3.7.2", {"start": v(105, 10) * mm, "end": v(105, 11) * mm});
            skLineSegment(sketch, "E3.6.7.2", {"start": v(115, 10) * mm, "end": v(115, 11) * mm});
            skLineSegment(sketch, "E3.9.7.2", {"start": v(105, 10) * mm, "end": v(115, 10) * mm});
            skLineSegment(sketch, "E3.0.7.3", {"start": v(105, 16) * mm, "end": v(115, 16) * mm});
            skLineSegment(sketch, "E3.3.7.3", {"start": v(105, 15) * mm, "end": v(105, 16) * mm});
            skLineSegment(sketch, "E3.6.7.3", {"start": v(115, 15) * mm, "end": v(115, 16) * mm});
            skLineSegment(sketch, "E3.9.7.3", {"start": v(105, 15) * mm, "end": v(115, 15) * mm});
            skLineSegment(sketch, "E3.0.7.4", {"start": v(105, 21) * mm, "end": v(115, 21) * mm});
            skLineSegment(sketch, "E3.3.7.4", {"start": v(105, 20) * mm, "end": v(105, 21) * mm});
            skLineSegment(sketch, "E3.6.7.4", {"start": v(115, 20) * mm, "end": v(115, 21) * mm});
            skLineSegment(sketch, "E3.9.7.4", {"start": v(105, 20) * mm, "end": v(115, 20) * mm});
            skLineSegment(sketch, "E3.0.7.5", {"start": v(105, 26) * mm, "end": v(115, 26) * mm});
            skLineSegment(sketch, "E3.3.7.5", {"start": v(105, 25) * mm, "end": v(105, 26) * mm});
            skLineSegment(sketch, "E3.6.7.5", {"start": v(115, 25) * mm, "end": v(115, 26) * mm});
            skLineSegment(sketch, "E3.9.7.5", {"start": v(105, 25) * mm, "end": v(115, 25) * mm});
            skLineSegment(sketch, "E3.0.7.6", {"start": v(105, 31) * mm, "end": v(115, 31) * mm});
            skLineSegment(sketch, "E3.3.7.6", {"start": v(105, 30) * mm, "end": v(105, 31) * mm});
            skLineSegment(sketch, "E3.6.7.6", {"start": v(115, 30) * mm, "end": v(115, 31) * mm});
            skLineSegment(sketch, "E3.9.7.6", {"start": v(105, 30) * mm, "end": v(115, 30) * mm});
            skLineSegment(sketch, "E3.0.7.7", {"start": v(105, 36) * mm, "end": v(115, 36) * mm});
            skLineSegment(sketch, "E3.3.7.7", {"start": v(105, 35) * mm, "end": v(105, 36) * mm});
            skLineSegment(sketch, "E3.6.7.7", {"start": v(115, 35) * mm, "end": v(115, 36) * mm});
            skLineSegment(sketch, "E3.9.7.7", {"start": v(105, 35) * mm, "end": v(115, 35) * mm});
            skLineSegment(sketch, "E3.0.7.8", {"start": v(105, 41) * mm, "end": v(115, 41) * mm});
            skLineSegment(sketch, "E3.3.7.8", {"start": v(105, 40) * mm, "end": v(105, 41) * mm});
            skLineSegment(sketch, "E3.6.7.8", {"start": v(115, 40) * mm, "end": v(115, 41) * mm});
            skLineSegment(sketch, "E3.9.7.8", {"start": v(105, 40) * mm, "end": v(115, 40) * mm});
            skLineSegment(sketch, "E3.0.7.9", {"start": v(105, 46) * mm, "end": v(115, 46) * mm});
            skLineSegment(sketch, "E3.3.7.9", {"start": v(105, 45) * mm, "end": v(105, 46) * mm});
            skLineSegment(sketch, "E3.6.7.9", {"start": v(115, 45) * mm, "end": v(115, 46) * mm});
            skLineSegment(sketch, "E3.9.7.9", {"start": v(105, 45) * mm, "end": v(115, 45) * mm});
            skLineSegment(sketch, "E3.0.8.2", {"start": v(120, 11) * mm, "end": v(130, 11) * mm});
            skLineSegment(sketch, "E3.3.8.2", {"start": v(120, 10) * mm, "end": v(120, 11) * mm});
            skLineSegment(sketch, "E3.6.8.2", {"start": v(130, 10) * mm, "end": v(130, 11) * mm});
            skLineSegment(sketch, "E3.9.8.2", {"start": v(120, 10) * mm, "end": v(130, 10) * mm});
            skLineSegment(sketch, "E3.0.8.3", {"start": v(120, 16) * mm, "end": v(130, 16) * mm});
            skLineSegment(sketch, "E3.3.8.3", {"start": v(120, 15) * mm, "end": v(120, 16) * mm});
            skLineSegment(sketch, "E3.6.8.3", {"start": v(130, 15) * mm, "end": v(130, 16) * mm});
            skLineSegment(sketch, "E3.9.8.3", {"start": v(120, 15) * mm, "end": v(130, 15) * mm});
            skLineSegment(sketch, "E3.0.8.4", {"start": v(120, 21) * mm, "end": v(130, 21) * mm});
            skLineSegment(sketch, "E3.3.8.4", {"start": v(120, 20) * mm, "end": v(120, 21) * mm});
            skLineSegment(sketch, "E3.6.8.4", {"start": v(130, 20) * mm, "end": v(130, 21) * mm});
            skLineSegment(sketch, "E3.9.8.4", {"start": v(120, 20) * mm, "end": v(130, 20) * mm});
            skLineSegment(sketch, "E3.0.8.5", {"start": v(120, 26) * mm, "end": v(130, 26) * mm});
            skLineSegment(sketch, "E3.3.8.5", {"start": v(120, 25) * mm, "end": v(120, 26) * mm});
            skLineSegment(sketch, "E3.6.8.5", {"start": v(130, 25) * mm, "end": v(130, 26) * mm});
            skLineSegment(sketch, "E3.9.8.5", {"start": v(120, 25) * mm, "end": v(130, 25) * mm});
            skLineSegment(sketch, "E3.0.8.6", {"start": v(120, 31) * mm, "end": v(130, 31) * mm});
            skLineSegment(sketch, "E3.3.8.6", {"start": v(120, 30) * mm, "end": v(120, 31) * mm});
            skLineSegment(sketch, "E3.6.8.6", {"start": v(130, 30) * mm, "end": v(130, 31) * mm});
            skLineSegment(sketch, "E3.9.8.6", {"start": v(120, 30) * mm, "end": v(130, 30) * mm});
            skLineSegment(sketch, "E3.0.8.7", {"start": v(120, 36) * mm, "end": v(130, 36) * mm});
            skLineSegment(sketch, "E3.3.8.7", {"start": v(120, 35) * mm, "end": v(120, 36) * mm});
            skLineSegment(sketch, "E3.6.8.7", {"start": v(130, 35) * mm, "end": v(130, 36) * mm});
            skLineSegment(sketch, "E3.9.8.7", {"start": v(120, 35) * mm, "end": v(130, 35) * mm});
            skLineSegment(sketch, "E3.0.8.8", {"start": v(120, 41) * mm, "end": v(130, 41) * mm});
            skLineSegment(sketch, "E3.3.8.8", {"start": v(120, 40) * mm, "end": v(120, 41) * mm});
            skLineSegment(sketch, "E3.6.8.8", {"start": v(130, 40) * mm, "end": v(130, 41) * mm});
            skLineSegment(sketch, "E3.9.8.8", {"start": v(120, 40) * mm, "end": v(130, 40) * mm});
            skLineSegment(sketch, "E3.0.8.9", {"start": v(120, 46) * mm, "end": v(130, 46) * mm});
            skLineSegment(sketch, "E3.3.8.9", {"start": v(120, 45) * mm, "end": v(120, 46) * mm});
            skLineSegment(sketch, "E3.6.8.9", {"start": v(130, 45) * mm, "end": v(130, 46) * mm});
            skLineSegment(sketch, "E3.9.8.9", {"start": v(120, 45) * mm, "end": v(130, 45) * mm});
            skLineSegment(sketch, "E3.0.9.2", {"start": v(135, 11) * mm, "end": v(145, 11) * mm});
            skLineSegment(sketch, "E3.3.9.2", {"start": v(135, 10) * mm, "end": v(135, 11) * mm});
            skLineSegment(sketch, "E3.6.9.2", {"start": v(145, 10) * mm, "end": v(145, 11) * mm});
            skLineSegment(sketch, "E3.9.9.2", {"start": v(135, 10) * mm, "end": v(145, 10) * mm});
            skLineSegment(sketch, "E3.0.9.3", {"start": v(135, 16) * mm, "end": v(145, 16) * mm});
            skLineSegment(sketch, "E3.3.9.3", {"start": v(135, 15) * mm, "end": v(135, 16) * mm});
            skLineSegment(sketch, "E3.6.9.3", {"start": v(145, 15) * mm, "end": v(145, 16) * mm});
            skLineSegment(sketch, "E3.9.9.3", {"start": v(135, 15) * mm, "end": v(145, 15) * mm});
            skLineSegment(sketch, "E3.0.9.4", {"start": v(135, 21) * mm, "end": v(145, 21) * mm});
            skLineSegment(sketch, "E3.3.9.4", {"start": v(135, 20) * mm, "end": v(135, 21) * mm});
            skLineSegment(sketch, "E3.6.9.4", {"start": v(145, 20) * mm, "end": v(145, 21) * mm});
            skLineSegment(sketch, "E3.9.9.4", {"start": v(135, 20) * mm, "end": v(145, 20) * mm});
            skLineSegment(sketch, "E3.0.9.5", {"start": v(135, 26) * mm, "end": v(145, 26) * mm});
            skLineSegment(sketch, "E3.3.9.5", {"start": v(135, 25) * mm, "end": v(135, 26) * mm});
            skLineSegment(sketch, "E3.6.9.5", {"start": v(145, 25) * mm, "end": v(145, 26) * mm});
            skLineSegment(sketch, "E3.9.9.5", {"start": v(135, 25) * mm, "end": v(145, 25) * mm});
            skLineSegment(sketch, "E3.0.9.6", {"start": v(135, 31) * mm, "end": v(145, 31) * mm});
            skLineSegment(sketch, "E3.3.9.6", {"start": v(135, 30) * mm, "end": v(135, 31) * mm});
            skLineSegment(sketch, "E3.6.9.6", {"start": v(145, 30) * mm, "end": v(145, 31) * mm});
            skLineSegment(sketch, "E3.9.9.6", {"start": v(135, 30) * mm, "end": v(145, 30) * mm});
            skLineSegment(sketch, "E3.0.9.7", {"start": v(135, 36) * mm, "end": v(145, 36) * mm});
            skLineSegment(sketch, "E3.3.9.7", {"start": v(135, 35) * mm, "end": v(135, 36) * mm});
            skLineSegment(sketch, "E3.6.9.7", {"start": v(145, 35) * mm, "end": v(145, 36) * mm});
            skLineSegment(sketch, "E3.9.9.7", {"start": v(135, 35) * mm, "end": v(145, 35) * mm});
            skLineSegment(sketch, "E3.0.9.8", {"start": v(135, 41) * mm, "end": v(145, 41) * mm});
            skLineSegment(sketch, "E3.3.9.8", {"start": v(135, 40) * mm, "end": v(135, 41) * mm});
            skLineSegment(sketch, "E3.6.9.8", {"start": v(145, 40) * mm, "end": v(145, 41) * mm});
            skLineSegment(sketch, "E3.9.9.8", {"start": v(135, 40) * mm, "end": v(145, 40) * mm});
            skLineSegment(sketch, "E3.0.9.9", {"start": v(135, 46) * mm, "end": v(145, 46) * mm});
            skLineSegment(sketch, "E3.3.9.9", {"start": v(135, 45) * mm, "end": v(135, 46) * mm});
            skLineSegment(sketch, "E3.6.9.9", {"start": v(145, 45) * mm, "end": v(145, 46) * mm});
            skLineSegment(sketch, "E3.9.9.9", {"start": v(135, 45) * mm, "end": v(145, 45) * mm});
            skLineSegment(sketch, "E4.0.0.10", {"start": v(0, 51) * mm, "end": v(10, 51) * mm});
            skLineSegment(sketch, "E4.3.0.10", {"start": v(0, 50) * mm, "end": v(0, 51) * mm});
            skLineSegment(sketch, "E4.6.0.10", {"start": v(10, 50) * mm, "end": v(10, 51) * mm});
            skLineSegment(sketch, "E4.9.0.10", {"start": v(0, 50) * mm, "end": v(10, 50) * mm});
            skLineSegment(sketch, "E4.0.0.11", {"start": v(0, 56) * mm, "end": v(10, 56) * mm});
            skLineSegment(sketch, "E4.3.0.11", {"start": v(0, 55) * mm, "end": v(0, 56) * mm});
            skLineSegment(sketch, "E4.6.0.11", {"start": v(10, 55) * mm, "end": v(10, 56) * mm});
            skLineSegment(sketch, "E4.9.0.11", {"start": v(0, 55) * mm, "end": v(10, 55) * mm});
            skLineSegment(sketch, "E4.0.0.12", {"start": v(0, 61) * mm, "end": v(10, 61) * mm});
            skLineSegment(sketch, "E4.3.0.12", {"start": v(0, 60) * mm, "end": v(0, 61) * mm});
            skLineSegment(sketch, "E4.6.0.12", {"start": v(10, 60) * mm, "end": v(10, 61) * mm});
            skLineSegment(sketch, "E4.9.0.12", {"start": v(0, 60) * mm, "end": v(10, 60) * mm});
            skLineSegment(sketch, "E4.0.0.13", {"start": v(0, 66) * mm, "end": v(10, 66) * mm});
            skLineSegment(sketch, "E4.3.0.13", {"start": v(0, 65) * mm, "end": v(0, 66) * mm});
            skLineSegment(sketch, "E4.6.0.13", {"start": v(10, 65) * mm, "end": v(10, 66) * mm});
            skLineSegment(sketch, "E4.9.0.13", {"start": v(0, 65) * mm, "end": v(10, 65) * mm});
            skLineSegment(sketch, "E4.0.0.14", {"start": v(0, 71) * mm, "end": v(10, 71) * mm});
            skLineSegment(sketch, "E4.3.0.14", {"start": v(0, 70) * mm, "end": v(0, 71) * mm});
            skLineSegment(sketch, "E4.6.0.14", {"start": v(10, 70) * mm, "end": v(10, 71) * mm});
            skLineSegment(sketch, "E4.9.0.14", {"start": v(0, 70) * mm, "end": v(10, 70) * mm});
            skLineSegment(sketch, "E4.0.1.10", {"start": v(15, 51) * mm, "end": v(25, 51) * mm});
            skLineSegment(sketch, "E4.3.1.10", {"start": v(15, 50) * mm, "end": v(15, 51) * mm});
            skLineSegment(sketch, "E4.6.1.10", {"start": v(25, 50) * mm, "end": v(25, 51) * mm});
            skLineSegment(sketch, "E4.9.1.10", {"start": v(15, 50) * mm, "end": v(25, 50) * mm});
            skLineSegment(sketch, "E4.0.1.11", {"start": v(15, 56) * mm, "end": v(25, 56) * mm});
            skLineSegment(sketch, "E4.3.1.11", {"start": v(15, 55) * mm, "end": v(15, 56) * mm});
            skLineSegment(sketch, "E4.6.1.11", {"start": v(25, 55) * mm, "end": v(25, 56) * mm});
            skLineSegment(sketch, "E4.9.1.11", {"start": v(15, 55) * mm, "end": v(25, 55) * mm});
            skLineSegment(sketch, "E4.0.1.12", {"start": v(15, 61) * mm, "end": v(25, 61) * mm});
            skLineSegment(sketch, "E4.3.1.12", {"start": v(15, 60) * mm, "end": v(15, 61) * mm});
            skLineSegment(sketch, "E4.6.1.12", {"start": v(25, 60) * mm, "end": v(25, 61) * mm});
            skLineSegment(sketch, "E4.9.1.12", {"start": v(15, 60) * mm, "end": v(25, 60) * mm});
            skLineSegment(sketch, "E4.0.1.13", {"start": v(15, 66) * mm, "end": v(25, 66) * mm});
            skLineSegment(sketch, "E4.3.1.13", {"start": v(15, 65) * mm, "end": v(15, 66) * mm});
            skLineSegment(sketch, "E4.6.1.13", {"start": v(25, 65) * mm, "end": v(25, 66) * mm});
            skLineSegment(sketch, "E4.9.1.13", {"start": v(15, 65) * mm, "end": v(25, 65) * mm});
            skLineSegment(sketch, "E4.0.1.14", {"start": v(15, 71) * mm, "end": v(25, 71) * mm});
            skLineSegment(sketch, "E4.3.1.14", {"start": v(15, 70) * mm, "end": v(15, 71) * mm});
            skLineSegment(sketch, "E4.6.1.14", {"start": v(25, 70) * mm, "end": v(25, 71) * mm});
            skLineSegment(sketch, "E4.9.1.14", {"start": v(15, 70) * mm, "end": v(25, 70) * mm});
            skLineSegment(sketch, "E4.0.2.10", {"start": v(30, 51) * mm, "end": v(40, 51) * mm});
            skLineSegment(sketch, "E4.3.2.10", {"start": v(30, 50) * mm, "end": v(30, 51) * mm});
            skLineSegment(sketch, "E4.6.2.10", {"start": v(40, 50) * mm, "end": v(40, 51) * mm});
            skLineSegment(sketch, "E4.9.2.10", {"start": v(30, 50) * mm, "end": v(40, 50) * mm});
            skLineSegment(sketch, "E4.0.2.11", {"start": v(30, 56) * mm, "end": v(40, 56) * mm});
            skLineSegment(sketch, "E4.3.2.11", {"start": v(30, 55) * mm, "end": v(30, 56) * mm});
            skLineSegment(sketch, "E4.6.2.11", {"start": v(40, 55) * mm, "end": v(40, 56) * mm});
            skLineSegment(sketch, "E4.9.2.11", {"start": v(30, 55) * mm, "end": v(40, 55) * mm});
            skLineSegment(sketch, "E4.0.2.12", {"start": v(30, 61) * mm, "end": v(40, 61) * mm});
            skLineSegment(sketch, "E4.3.2.12", {"start": v(30, 60) * mm, "end": v(30, 61) * mm});
            skLineSegment(sketch, "E4.6.2.12", {"start": v(40, 60) * mm, "end": v(40, 61) * mm});
            skLineSegment(sketch, "E4.9.2.12", {"start": v(30, 60) * mm, "end": v(40, 60) * mm});
            skLineSegment(sketch, "E4.0.2.13", {"start": v(30, 66) * mm, "end": v(40, 66) * mm});
            skLineSegment(sketch, "E4.3.2.13", {"start": v(30, 65) * mm, "end": v(30, 66) * mm});
            skLineSegment(sketch, "E4.6.2.13", {"start": v(40, 65) * mm, "end": v(40, 66) * mm});
            skLineSegment(sketch, "E4.9.2.13", {"start": v(30, 65) * mm, "end": v(40, 65) * mm});
            skLineSegment(sketch, "E4.0.2.14", {"start": v(30, 71) * mm, "end": v(40, 71) * mm});
            skLineSegment(sketch, "E4.3.2.14", {"start": v(30, 70) * mm, "end": v(30, 71) * mm});
            skLineSegment(sketch, "E4.6.2.14", {"start": v(40, 70) * mm, "end": v(40, 71) * mm});
            skLineSegment(sketch, "E4.9.2.14", {"start": v(30, 70) * mm, "end": v(40, 70) * mm});
            skLineSegment(sketch, "E4.0.3.10", {"start": v(45, 51) * mm, "end": v(55, 51) * mm});
            skLineSegment(sketch, "E4.3.3.10", {"start": v(45, 50) * mm, "end": v(45, 51) * mm});
            skLineSegment(sketch, "E4.6.3.10", {"start": v(55, 50) * mm, "end": v(55, 51) * mm});
            skLineSegment(sketch, "E4.9.3.10", {"start": v(45, 50) * mm, "end": v(55, 50) * mm});
            skLineSegment(sketch, "E4.0.3.11", {"start": v(45, 56) * mm, "end": v(55, 56) * mm});
            skLineSegment(sketch, "E4.3.3.11", {"start": v(45, 55) * mm, "end": v(45, 56) * mm});
            skLineSegment(sketch, "E4.6.3.11", {"start": v(55, 55) * mm, "end": v(55, 56) * mm});
            skLineSegment(sketch, "E4.9.3.11", {"start": v(45, 55) * mm, "end": v(55, 55) * mm});
            skLineSegment(sketch, "E4.0.3.12", {"start": v(45, 61) * mm, "end": v(55, 61) * mm});
            skLineSegment(sketch, "E4.3.3.12", {"start": v(45, 60) * mm, "end": v(45, 61) * mm});
            skLineSegment(sketch, "E4.6.3.12", {"start": v(55, 60) * mm, "end": v(55, 61) * mm});
            skLineSegment(sketch, "E4.9.3.12", {"start": v(45, 60) * mm, "end": v(55, 60) * mm});
            skLineSegment(sketch, "E4.0.3.13", {"start": v(45, 66) * mm, "end": v(55, 66) * mm});
            skLineSegment(sketch, "E4.3.3.13", {"start": v(45, 65) * mm, "end": v(45, 66) * mm});
            skLineSegment(sketch, "E4.6.3.13", {"start": v(55, 65) * mm, "end": v(55, 66) * mm});
            skLineSegment(sketch, "E4.9.3.13", {"start": v(45, 65) * mm, "end": v(55, 65) * mm});
            skLineSegment(sketch, "E4.0.3.14", {"start": v(45, 71) * mm, "end": v(55, 71) * mm});
            skLineSegment(sketch, "E4.3.3.14", {"start": v(45, 70) * mm, "end": v(45, 71) * mm});
            skLineSegment(sketch, "E4.6.3.14", {"start": v(55, 70) * mm, "end": v(55, 71) * mm});
            skLineSegment(sketch, "E4.9.3.14", {"start": v(45, 70) * mm, "end": v(55, 70) * mm});
            skLineSegment(sketch, "E4.0.4.10", {"start": v(60, 51) * mm, "end": v(70, 51) * mm});
            skLineSegment(sketch, "E4.3.4.10", {"start": v(60, 50) * mm, "end": v(60, 51) * mm});
            skLineSegment(sketch, "E4.6.4.10", {"start": v(70, 50) * mm, "end": v(70, 51) * mm});
            skLineSegment(sketch, "E4.9.4.10", {"start": v(60, 50) * mm, "end": v(70, 50) * mm});
            skLineSegment(sketch, "E4.0.4.11", {"start": v(60, 56) * mm, "end": v(70, 56) * mm});
            skLineSegment(sketch, "E4.3.4.11", {"start": v(60, 55) * mm, "end": v(60, 56) * mm});
            skLineSegment(sketch, "E4.6.4.11", {"start": v(70, 55) * mm, "end": v(70, 56) * mm});
            skLineSegment(sketch, "E4.9.4.11", {"start": v(60, 55) * mm, "end": v(70, 55) * mm});
            skLineSegment(sketch, "E4.0.4.12", {"start": v(60, 61) * mm, "end": v(70, 61) * mm});
            skLineSegment(sketch, "E4.3.4.12", {"start": v(60, 60) * mm, "end": v(60, 61) * mm});
            skLineSegment(sketch, "E4.6.4.12", {"start": v(70, 60) * mm, "end": v(70, 61) * mm});
            skLineSegment(sketch, "E4.9.4.12", {"start": v(60, 60) * mm, "end": v(70, 60) * mm});
            skLineSegment(sketch, "E4.0.4.13", {"start": v(60, 66) * mm, "end": v(70, 66) * mm});
            skLineSegment(sketch, "E4.3.4.13", {"start": v(60, 65) * mm, "end": v(60, 66) * mm});
            skLineSegment(sketch, "E4.6.4.13", {"start": v(70, 65) * mm, "end": v(70, 66) * mm});
            skLineSegment(sketch, "E4.9.4.13", {"start": v(60, 65) * mm, "end": v(70, 65) * mm});
            skLineSegment(sketch, "E4.0.4.14", {"start": v(60, 71) * mm, "end": v(70, 71) * mm});
            skLineSegment(sketch, "E4.3.4.14", {"start": v(60, 70) * mm, "end": v(60, 71) * mm});
            skLineSegment(sketch, "E4.6.4.14", {"start": v(70, 70) * mm, "end": v(70, 71) * mm});
            skLineSegment(sketch, "E4.9.4.14", {"start": v(60, 70) * mm, "end": v(70, 70) * mm});
            skLineSegment(sketch, "E4.0.5.10", {"start": v(75, 51) * mm, "end": v(85, 51) * mm});
            skLineSegment(sketch, "E4.3.5.10", {"start": v(75, 50) * mm, "end": v(75, 51) * mm});
            skLineSegment(sketch, "E4.6.5.10", {"start": v(85, 50) * mm, "end": v(85, 51) * mm});
            skLineSegment(sketch, "E4.9.5.10", {"start": v(75, 50) * mm, "end": v(85, 50) * mm});
            skLineSegment(sketch, "E4.0.5.11", {"start": v(75, 56) * mm, "end": v(85, 56) * mm});
            skLineSegment(sketch, "E4.3.5.11", {"start": v(75, 55) * mm, "end": v(75, 56) * mm});
            skLineSegment(sketch, "E4.6.5.11", {"start": v(85, 55) * mm, "end": v(85, 56) * mm});
            skLineSegment(sketch, "E4.9.5.11", {"start": v(75, 55) * mm, "end": v(85, 55) * mm});
            skLineSegment(sketch, "E4.0.5.12", {"start": v(75, 61) * mm, "end": v(85, 61) * mm});
            skLineSegment(sketch, "E4.3.5.12", {"start": v(75, 60) * mm, "end": v(75, 61) * mm});
            skLineSegment(sketch, "E4.6.5.12", {"start": v(85, 60) * mm, "end": v(85, 61) * mm});
            skLineSegment(sketch, "E4.9.5.12", {"start": v(75, 60) * mm, "end": v(85, 60) * mm});
            skLineSegment(sketch, "E4.0.5.13", {"start": v(75, 66) * mm, "end": v(85, 66) * mm});
            skLineSegment(sketch, "E4.3.5.13", {"start": v(75, 65) * mm, "end": v(75, 66) * mm});
            skLineSegment(sketch, "E4.6.5.13", {"start": v(85, 65) * mm, "end": v(85, 66) * mm});
            skLineSegment(sketch, "E4.9.5.13", {"start": v(75, 65) * mm, "end": v(85, 65) * mm});
            skLineSegment(sketch, "E4.0.5.14", {"start": v(75, 71) * mm, "end": v(85, 71) * mm});
            skLineSegment(sketch, "E4.3.5.14", {"start": v(75, 70) * mm, "end": v(75, 71) * mm});
            skLineSegment(sketch, "E4.6.5.14", {"start": v(85, 70) * mm, "end": v(85, 71) * mm});
            skLineSegment(sketch, "E4.9.5.14", {"start": v(75, 70) * mm, "end": v(85, 70) * mm});
            skLineSegment(sketch, "E4.0.6.10", {"start": v(90, 51) * mm, "end": v(100, 51) * mm});
            skLineSegment(sketch, "E4.3.6.10", {"start": v(90, 50) * mm, "end": v(90, 51) * mm});
            skLineSegment(sketch, "E4.6.6.10", {"start": v(100, 50) * mm, "end": v(100, 51) * mm});
            skLineSegment(sketch, "E4.9.6.10", {"start": v(90, 50) * mm, "end": v(100, 50) * mm});
            skLineSegment(sketch, "E4.0.6.11", {"start": v(90, 56) * mm, "end": v(100, 56) * mm});
            skLineSegment(sketch, "E4.3.6.11", {"start": v(90, 55) * mm, "end": v(90, 56) * mm});
            skLineSegment(sketch, "E4.6.6.11", {"start": v(100, 55) * mm, "end": v(100, 56) * mm});
            skLineSegment(sketch, "E4.9.6.11", {"start": v(90, 55) * mm, "end": v(100, 55) * mm});
            skLineSegment(sketch, "E4.0.6.12", {"start": v(90, 61) * mm, "end": v(100, 61) * mm});
            skLineSegment(sketch, "E4.3.6.12", {"start": v(90, 60) * mm, "end": v(90, 61) * mm});
            skLineSegment(sketch, "E4.6.6.12", {"start": v(100, 60) * mm, "end": v(100, 61) * mm});
            skLineSegment(sketch, "E4.9.6.12", {"start": v(90, 60) * mm, "end": v(100, 60) * mm});
            skLineSegment(sketch, "E4.0.6.13", {"start": v(90, 66) * mm, "end": v(100, 66) * mm});
            skLineSegment(sketch, "E4.3.6.13", {"start": v(90, 65) * mm, "end": v(90, 66) * mm});
            skLineSegment(sketch, "E4.6.6.13", {"start": v(100, 65) * mm, "end": v(100, 66) * mm});
            skLineSegment(sketch, "E4.9.6.13", {"start": v(90, 65) * mm, "end": v(100, 65) * mm});
            skLineSegment(sketch, "E4.0.6.14", {"start": v(90, 71) * mm, "end": v(100, 71) * mm});
            skLineSegment(sketch, "E4.3.6.14", {"start": v(90, 70) * mm, "end": v(90, 71) * mm});
            skLineSegment(sketch, "E4.6.6.14", {"start": v(100, 70) * mm, "end": v(100, 71) * mm});
            skLineSegment(sketch, "E4.9.6.14", {"start": v(90, 70) * mm, "end": v(100, 70) * mm});
            skLineSegment(sketch, "E4.0.7.10", {"start": v(105, 51) * mm, "end": v(115, 51) * mm});
            skLineSegment(sketch, "E4.3.7.10", {"start": v(105, 50) * mm, "end": v(105, 51) * mm});
            skLineSegment(sketch, "E4.6.7.10", {"start": v(115, 50) * mm, "end": v(115, 51) * mm});
            skLineSegment(sketch, "E4.9.7.10", {"start": v(105, 50) * mm, "end": v(115, 50) * mm});
            skLineSegment(sketch, "E4.0.7.11", {"start": v(105, 56) * mm, "end": v(115, 56) * mm});
            skLineSegment(sketch, "E4.3.7.11", {"start": v(105, 55) * mm, "end": v(105, 56) * mm});
            skLineSegment(sketch, "E4.6.7.11", {"start": v(115, 55) * mm, "end": v(115, 56) * mm});
            skLineSegment(sketch, "E4.9.7.11", {"start": v(105, 55) * mm, "end": v(115, 55) * mm});
            skLineSegment(sketch, "E4.0.7.12", {"start": v(105, 61) * mm, "end": v(115, 61) * mm});
            skLineSegment(sketch, "E4.3.7.12", {"start": v(105, 60) * mm, "end": v(105, 61) * mm});
            skLineSegment(sketch, "E4.6.7.12", {"start": v(115, 60) * mm, "end": v(115, 61) * mm});
            skLineSegment(sketch, "E4.9.7.12", {"start": v(105, 60) * mm, "end": v(115, 60) * mm});
            skLineSegment(sketch, "E4.0.7.13", {"start": v(105, 66) * mm, "end": v(115, 66) * mm});
            skLineSegment(sketch, "E4.3.7.13", {"start": v(105, 65) * mm, "end": v(105, 66) * mm});
            skLineSegment(sketch, "E4.6.7.13", {"start": v(115, 65) * mm, "end": v(115, 66) * mm});
            skLineSegment(sketch, "E4.9.7.13", {"start": v(105, 65) * mm, "end": v(115, 65) * mm});
            skLineSegment(sketch, "E4.0.7.14", {"start": v(105, 71) * mm, "end": v(115, 71) * mm});
            skLineSegment(sketch, "E4.3.7.14", {"start": v(105, 70) * mm, "end": v(105, 71) * mm});
            skLineSegment(sketch, "E4.6.7.14", {"start": v(115, 70) * mm, "end": v(115, 71) * mm});
            skLineSegment(sketch, "E4.9.7.14", {"start": v(105, 70) * mm, "end": v(115, 70) * mm});
            skLineSegment(sketch, "E4.0.8.10", {"start": v(120, 51) * mm, "end": v(130, 51) * mm});
            skLineSegment(sketch, "E4.3.8.10", {"start": v(120, 50) * mm, "end": v(120, 51) * mm});
            skLineSegment(sketch, "E4.6.8.10", {"start": v(130, 50) * mm, "end": v(130, 51) * mm});
            skLineSegment(sketch, "E4.9.8.10", {"start": v(120, 50) * mm, "end": v(130, 50) * mm});
            skLineSegment(sketch, "E4.0.8.11", {"start": v(120, 56) * mm, "end": v(130, 56) * mm});
            skLineSegment(sketch, "E4.3.8.11", {"start": v(120, 55) * mm, "end": v(120, 56) * mm});
            skLineSegment(sketch, "E4.6.8.11", {"start": v(130, 55) * mm, "end": v(130, 56) * mm});
            skLineSegment(sketch, "E4.9.8.11", {"start": v(120, 55) * mm, "end": v(130, 55) * mm});
            skLineSegment(sketch, "E4.0.8.12", {"start": v(120, 61) * mm, "end": v(130, 61) * mm});
            skLineSegment(sketch, "E4.3.8.12", {"start": v(120, 60) * mm, "end": v(120, 61) * mm});
            skLineSegment(sketch, "E4.6.8.12", {"start": v(130, 60) * mm, "end": v(130, 61) * mm});
            skLineSegment(sketch, "E4.9.8.12", {"start": v(120, 60) * mm, "end": v(130, 60) * mm});
            skLineSegment(sketch, "E4.0.8.13", {"start": v(120, 66) * mm, "end": v(130, 66) * mm});
            skLineSegment(sketch, "E4.3.8.13", {"start": v(120, 65) * mm, "end": v(120, 66) * mm});
            skLineSegment(sketch, "E4.6.8.13", {"start": v(130, 65) * mm, "end": v(130, 66) * mm});
            skLineSegment(sketch, "E4.9.8.13", {"start": v(120, 65) * mm, "end": v(130, 65) * mm});
            skLineSegment(sketch, "E4.0.8.14", {"start": v(120, 71) * mm, "end": v(130, 71) * mm});
            skLineSegment(sketch, "E4.3.8.14", {"start": v(120, 70) * mm, "end": v(120, 71) * mm});
            skLineSegment(sketch, "E4.6.8.14", {"start": v(130, 70) * mm, "end": v(130, 71) * mm});
            skLineSegment(sketch, "E4.9.8.14", {"start": v(120, 70) * mm, "end": v(130, 70) * mm});
            skLineSegment(sketch, "E4.0.9.10", {"start": v(135, 51) * mm, "end": v(145, 51) * mm});
            skLineSegment(sketch, "E4.3.9.10", {"start": v(135, 50) * mm, "end": v(135, 51) * mm});
            skLineSegment(sketch, "E4.6.9.10", {"start": v(145, 50) * mm, "end": v(145, 51) * mm});
            skLineSegment(sketch, "E4.9.9.10", {"start": v(135, 50) * mm, "end": v(145, 50) * mm});
            skLineSegment(sketch, "E4.0.9.11", {"start": v(135, 56) * mm, "end": v(145, 56) * mm});
            skLineSegment(sketch, "E4.3.9.11", {"start": v(135, 55) * mm, "end": v(135, 56) * mm});
            skLineSegment(sketch, "E4.6.9.11", {"start": v(145, 55) * mm, "end": v(145, 56) * mm});
            skLineSegment(sketch, "E4.9.9.11", {"start": v(135, 55) * mm, "end": v(145, 55) * mm});
            skLineSegment(sketch, "E4.0.9.12", {"start": v(135, 61) * mm, "end": v(145, 61) * mm});
            skLineSegment(sketch, "E4.3.9.12", {"start": v(135, 60) * mm, "end": v(135, 61) * mm});
            skLineSegment(sketch, "E4.6.9.12", {"start": v(145, 60) * mm, "end": v(145, 61) * mm});
            skLineSegment(sketch, "E4.9.9.12", {"start": v(135, 60) * mm, "end": v(145, 60) * mm});
            skLineSegment(sketch, "E4.0.9.13", {"start": v(135, 66) * mm, "end": v(145, 66) * mm});
            skLineSegment(sketch, "E4.3.9.13", {"start": v(135, 65) * mm, "end": v(135, 66) * mm});
            skLineSegment(sketch, "E4.6.9.13", {"start": v(145, 65) * mm, "end": v(145, 66) * mm});
            skLineSegment(sketch, "E4.9.9.13", {"start": v(135, 65) * mm, "end": v(145, 65) * mm});
            skLineSegment(sketch, "E4.0.9.14", {"start": v(135, 71) * mm, "end": v(145, 71) * mm});
            skLineSegment(sketch, "E4.3.9.14", {"start": v(135, 70) * mm, "end": v(135, 71) * mm});
            skLineSegment(sketch, "E4.6.9.14", {"start": v(145, 70) * mm, "end": v(145, 71) * mm});
            skLineSegment(sketch, "E4.9.9.14", {"start": v(135, 70) * mm, "end": v(145, 70) * mm});
            skSolve(sketch);
        }
        {
            var Q0;
            Q0 = qSketchRegion(id + "F0", true);
            extrude(context, id + "F1", {"entities" : qUnion([Q0]), "depth" : 0.5 * mm});
        }
    });
